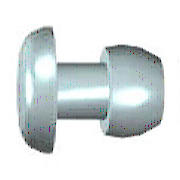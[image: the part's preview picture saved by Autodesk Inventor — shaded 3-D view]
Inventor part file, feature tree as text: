
AUTODESK INVENTOR PART (.ipt)
format: ipt  version: 2024.2 (Build 282272000, 272)  size: 171,008 bytes
history: native  units: mm
features: revolve x1, sketch x1
ambient origin geometry x8: Origin, YZ Plane, XZ Plane, XY Plane, X Axis, Y Axis, Z Axis, Center Point
bodies: Body1 (feature_tree)
feature tree (2):
  revolve  "Revolution 1"  [1 undecoded]
  sketch  "Sketch1"  dims[d16=90.0deg d21=2.0mm d22=5.555mm d23=7.272mm d27=6.0mm d28=10.1mm]
note: 1 required parameter value undecoded (feature->parameter linkage not recoverable at this tier; creation-order binding heuristic only, values carry confidence <= 0.55)
